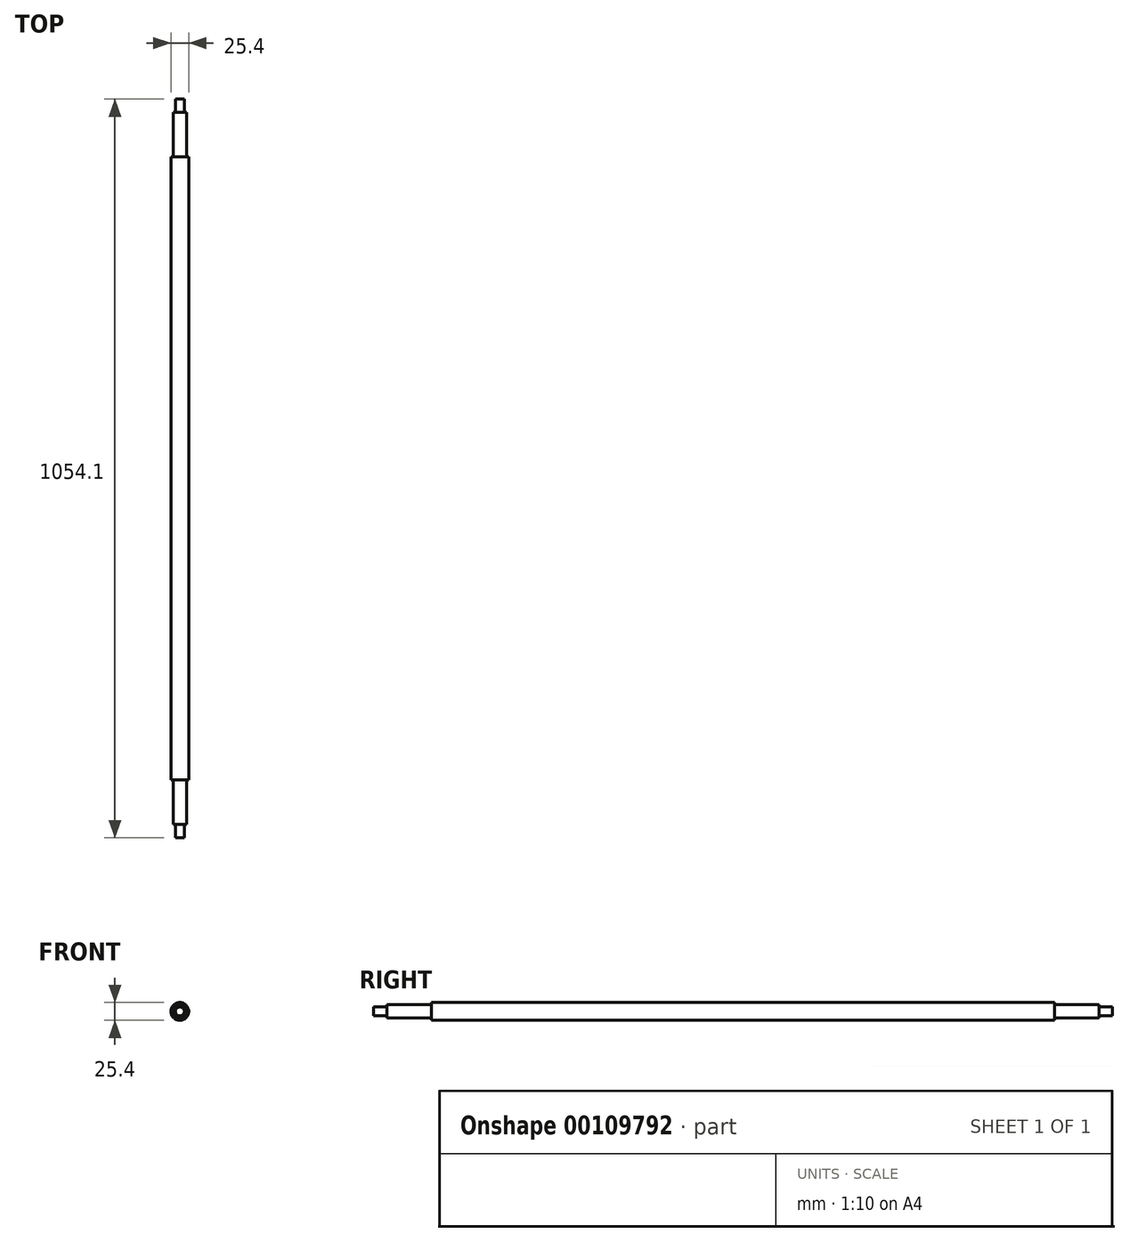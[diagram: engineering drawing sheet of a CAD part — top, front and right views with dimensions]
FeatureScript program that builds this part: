
annotation { "Feature Type Name" : "Feature", "Feature Type Description" : "" }
export const myFeature = defineFeature(function(context is Context, id is Id, definition is map)
    precondition{}
    {
        {
            var Q0;
            Q0=qCreatedBy(makeId("Right.planeOp"),FACE);
            var sketch = newSketch(context, id + "F0", { "sketchPlane" : qUnion([Q0])});
            skLineSegment(sketch, "E0", {"start": v(889, 169.12) * mm, "end": v(889, -55.03) * mm});
            skLineSegment(sketch, "E1.top", {"start": v(-25.4, -9.52) * mm, "end": v(38.1, -9.52) * mm});
            skLineSegment(sketch, "E2", {"start": v(-44.45, 0) * mm, "end": v(-44.45, -6.35) * mm});
            skLineSegment(sketch, "E3", {"start": v(-44.45, 0) * mm, "end": v(482.6, 0) * mm});
            skPoint(sketch, "E3.startSnap0", {"position": v(127, 0) * mm});
            skLineSegment(sketch, "E4.trimOffspring", {"start": v(-25.4, -6.35) * mm, "end": v(-44.45, -6.35) * mm});
            skLineSegment(sketch, "E5", {"start": v(-25.4, -6.35) * mm, "end": v(-25.4, -9.53) * mm});
            skLineSegment(sketch, "E6", {"start": v(38.1, -9.53) * mm, "end": v(38.1, -12.7) * mm});
            skLineSegment(sketch, "E7", {"start": v(38.1, -12.7) * mm, "end": v(482.6, -12.7) * mm});
            skLineSegment(sketch, "E8", {"start": v(482.6, -12.7) * mm, "end": v(482.6, 0) * mm});
            skSolve(sketch);
        }
        {
            var Q0;
            Q0=qCreatedBy(makeId("Front.planeOp"),FACE);
            var sketch = newSketch(context, id + "F1", { "sketchPlane" : qUnion([Q0])});
            skCircle(sketch, "E9", {"center": v(0, 0) * mm, "radius": 17.2 * mm});
            skSolve(sketch);
        }
        {
            var Q0;
            Q0=sQuery(id+"F0.wireOp",VERTEX,"E3.end");
            var Q1;
            Q1=sQuery(id+"F0.wireOp",EDGE,"E3");
            cPlane(context, id + "F2", {"entities" : qUnion([Q0, Q1]), "cplaneType" : CPlaneType.LINE_POINT, "offset" : 25.4 * mm, "width" : 152.4 * mm, "height" : 152.4 * mm});
        }
        {
            var Q0;
            Q0=makeQuery(id+"F0.imprint","IMPRINT",FACE,{"disambiguationData":[TD([[makeQuery(id+"F0.imprint","IMPRINT",EDGE,{"derivedFrom":sQuery(id+"F0.wireOp",EDGE,"E1.top")}),1.0]])]});
            var Q1;
            Q1=sQuery(id+"F1.wireOp",EDGE,"E9");
            sweep(context, id + "F3", {"profiles" : qUnion([Q0]), "path" : qUnion([Q1])});
        }
        {
            var Q0;
            Q0=makeQuery(id+"F3.opSweep","SWEPT_BODY",BODY,{"disambiguationData":[OSD([sQuery(id+"F0.wireOp",EDGE,"E1.top"),sQuery(id+"F0.wireOp",EDGE,"E2"),sQuery(id+"F0.wireOp",EDGE,"E3"),sQuery(id+"F0.wireOp",EDGE,"E4.trimOffspring"),sQuery(id+"F0.wireOp",EDGE,"E5"),sQuery(id+"F0.wireOp",EDGE,"E6"),sQuery(id+"F0.wireOp",EDGE,"E7"),sQuery(id+"F0.wireOp",EDGE,"E8"),sQuery(id+"F1.wireOp",EDGE,"E9")])]});
            var Q1;
            Q1=qCreatedBy(id+"F2.planeOp",FACE);
            mirror(context, id + "F4", {"operationType" : NewBodyOperationType.ADD, "entities" : qUnion([Q0]), "mirrorPlane" : qUnion([Q1])});
        }
    });
